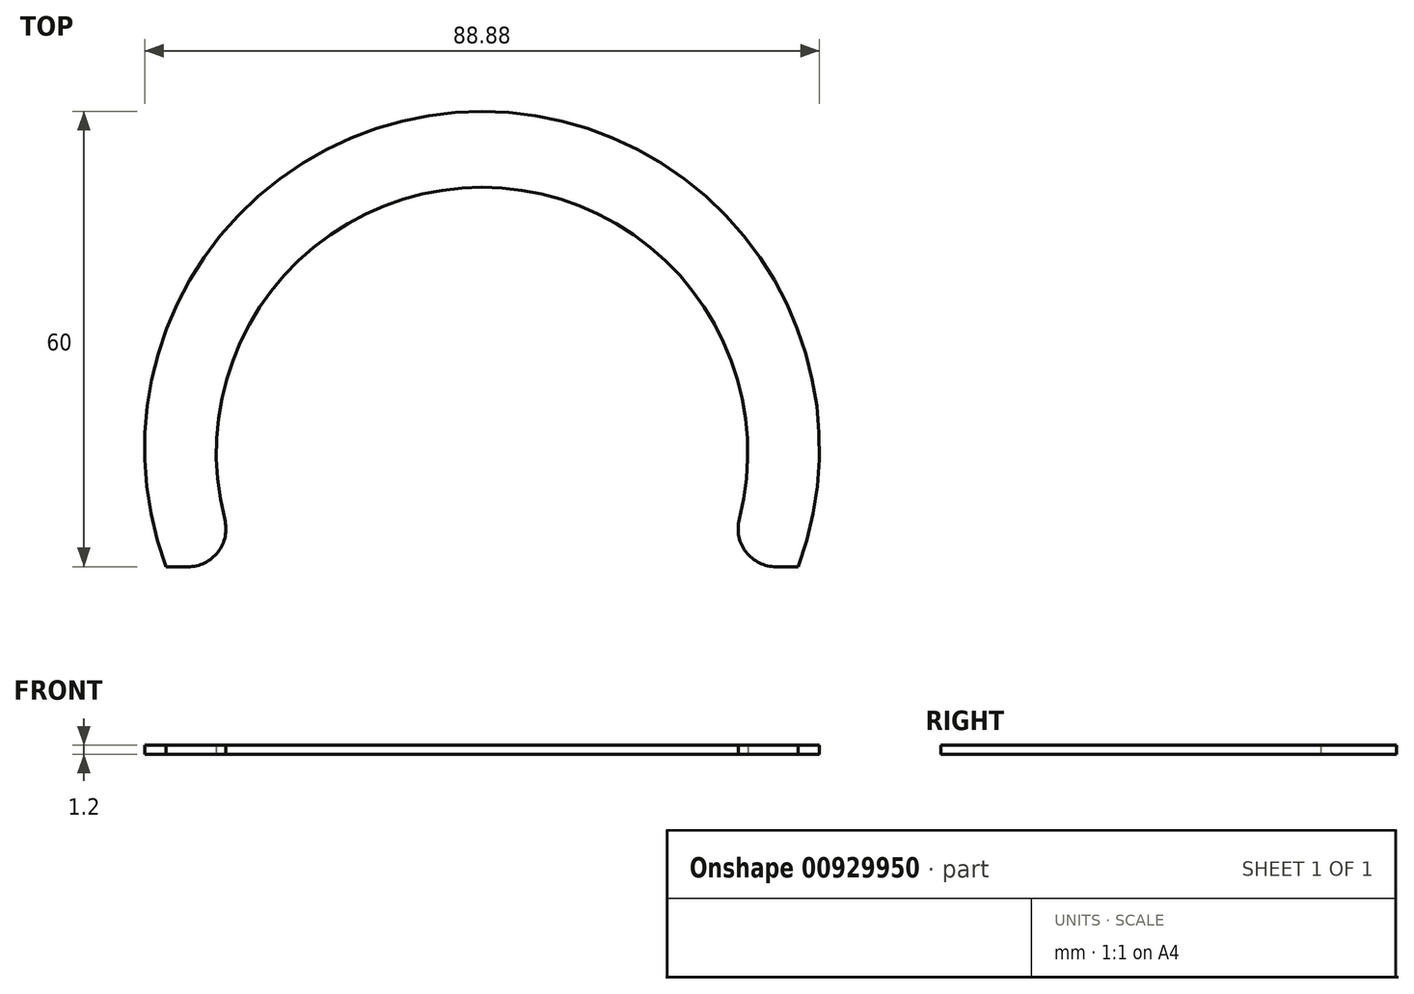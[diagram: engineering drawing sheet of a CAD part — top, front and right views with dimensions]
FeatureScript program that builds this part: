
annotation { "Feature Type Name" : "Feature", "Feature Type Description" : "" }
export const myFeature = defineFeature(function(context is Context, id is Id, definition is map)
    precondition{}
    {
        {
            var Q0;
            Q0=qCreatedBy(makeId("Top.planeOp"),FACE);
            var sketch = newSketch(context, id + "F0", { "sketchPlane" : qUnion([Q0])});
            skCircle(sketch, "E0", {"center": v(0, 0) * mm, "radius": 35 * mm, "construction": true});
            skPoint(sketch, "E1", {"position": v(-35, 0) * mm});
            skPoint(sketch, "E2", {"position": v(35, 0) * mm});
            skPoint(sketch, "E3", {"position": v(0, 35) * mm});
            skArc(sketch, "E4", {"start": v(31.62, -15) * mm, "mid": v(0, 35) * mm, "end": v(-31.62, -15) * mm});
            skLineSegment(sketch, "E5", {"start": v(-31.62, -15) * mm, "end": v(31.62, -15) * mm, "construction": true});
            skLineSegment(sketch, "E6", {"start": v(0, 0) * mm, "end": v(0, -15) * mm, "construction": true});
            skLineSegment(sketch, "E7", {"start": v(-31.62, -15) * mm, "end": v(-41.62, -15) * mm});
            skLineSegment(sketch, "E8", {"start": v(31.62, -15) * mm, "end": v(41.62, -15) * mm});
            skLineSegment(sketch, "E9", {"start": v(0, 45) * mm, "end": v(0, 35) * mm, "construction": true});
            skArc(sketch, "E10", {"start": v(41.62, -15) * mm, "mid": v(0, 45) * mm, "end": v(-41.62, -15) * mm});
            skSolve(sketch);
        }
        {
            var Q0;
            Q0 = qSketchRegion(id + "F0", true);
            extrude(context, id + "F1", {"entities" : qUnion([Q0]), "depth" : 1.2 * mm, "offsetDistance" : 25 * mm});
        }
        {
            var Q0;
            Q0=makeQuery(id+"F1.opExtrude","CAP_FACE",FACE,{"disambiguationData":[OSD([sQuery(id+"F0.wireOp",EDGE,"E4"),sQuery(id+"F0.wireOp",EDGE,"E7"),sQuery(id+"F0.wireOp",EDGE,"E8"),sQuery(id+"F0.wireOp",EDGE,"E10")])],"isStart":false});
            var sketch = newSketch(context, id + "F2", { "sketchPlane" : qUnion([Q0])});
            skArc(sketch, "E11.0", {"start": v(31.62, -15) * mm, "mid": v(0, 35) * mm, "end": v(-31.62, -15) * mm});
            skLineSegment(sketch, "E12", {"start": v(-31.62, -15) * mm, "end": v(-32.82, -15) * mm});
            skLineSegment(sketch, "E13", {"start": v(31.62, -15) * mm, "end": v(32.82, -15) * mm});
            skLineSegment(sketch, "E14", {"start": v(0, 35) * mm, "end": v(0, 36.2) * mm, "construction": true});
            skArc(sketch, "E15", {"start": v(32.82, -15) * mm, "mid": v(0, 36.2) * mm, "end": v(-32.82, -15) * mm});
            skSolve(sketch);
        }
        {
            var Q0;
            Q0 = qSketchRegion(id + "F2", true);
            extrude(context, id + "F3", {"entities" : qUnion([Q0]), "operationType" : NewBodyOperationType.ADD, "depth" : 10 * mm, "offsetDistance" : 25 * mm});
        }
        {
            var Q0;
            Q0=makeQuery(id+"F1.opExtrude","CAP_FACE",FACE,{"disambiguationData":[OSD([sQuery(id+"F0.wireOp",EDGE,"E4"),sQuery(id+"F0.wireOp",EDGE,"E7"),sQuery(id+"F0.wireOp",EDGE,"E8"),sQuery(id+"F0.wireOp",EDGE,"E10")])],"isStart":false});
            var sketch = newSketch(context, id + "F4", { "sketchPlane" : qUnion([Q0])});
            skArc(sketch, "E16.0", {"start": v(41.62, -15) * mm, "mid": v(0, 45) * mm, "end": v(-41.62, -15) * mm});
            skLineSegment(sketch, "E17", {"start": v(-41.62, -15) * mm, "end": v(-40.82, -15) * mm});
            skLineSegment(sketch, "E18", {"start": v(41.62, -15) * mm, "end": v(40.82, -15) * mm});
            skLineSegment(sketch, "E19", {"start": v(0, 45) * mm, "end": v(0, 44.2) * mm, "construction": true});
            skArc(sketch, "E20", {"start": v(40.82, -15) * mm, "mid": v(0, 44.2) * mm, "end": v(-40.82, -15) * mm});
            skSolve(sketch);
        }
        {
            var Q0;
            Q0 = qSketchRegion(id + "F4", true);
            extrude(context, id + "F5", {"entities" : qUnion([Q0]), "operationType" : NewBodyOperationType.ADD, "depth" : 135 * mm, "offsetDistance" : 25 * mm});
        }
        {
            var Q0;
            Q0=makeQuery(id+"F3.boolean.opBoolean","MERGE",EDGE,{"derivedFrom":[makeQuery(id+"F1.opExtrude","SWEPT_EDGE",EDGE,{"disambiguationData":[OSD([sQuery(id+"F0.wireOp",EDGE,"E4"),sQuery(id+"F0.wireOp",EDGE,"E7")])]}),makeQuery(id+"F3.opExtrude","SWEPT_EDGE",EDGE,{"disambiguationData":[OSD([sQuery(id+"F2.wireOp",EDGE,"E11.0"),sQuery(id+"F2.wireOp",EDGE,"E12")])]})]});
            var Q1;
            Q1=makeQuery(id+"F3.boolean.opBoolean","MERGE",EDGE,{"derivedFrom":[makeQuery(id+"F1.opExtrude","SWEPT_EDGE",EDGE,{"disambiguationData":[OSD([sQuery(id+"F0.wireOp",EDGE,"E4"),sQuery(id+"F0.wireOp",EDGE,"E8")])]}),makeQuery(id+"F3.opExtrude","SWEPT_EDGE",EDGE,{"disambiguationData":[OSD([sQuery(id+"F2.wireOp",EDGE,"E11.0"),sQuery(id+"F2.wireOp",EDGE,"E13")])]})]});
            fillet(context, id + "F6", {"entities" : qUnion([Q0, Q1]), "radius" : 5 * mm, "tangentPropagation" : true, "allowEdgeOverflow" : false});
        }
        {
            var Q0;
            Q0=qCreatedBy(makeId("Top.planeOp"),FACE);
            var sketch = newSketch(context, id + "F7", { "sketchPlane" : qUnion([Q0])});
            skCircle(sketch, "E21", {"center": v(0, 0) * mm, "radius": 63.74 * mm});
            skSolve(sketch);
        }
        {
            var Q0;
            Q0 = qSketchRegion(id + "F7", true);
            var Q1;
            Q1=makeQuery(id+"F1.opExtrude","CAP_FACE",FACE,{"disambiguationData":[OSD([sQuery(id+"F0.wireOp",EDGE,"E4"),sQuery(id+"F0.wireOp",EDGE,"E7"),sQuery(id+"F0.wireOp",EDGE,"E8"),sQuery(id+"F0.wireOp",EDGE,"E10")])],"isStart":false});
            extrude(context, id + "F8", {"entities" : qUnion([Q0]), "endBound" : BoundingType.UP_TO_SURFACE, "depth" : 25 * mm, "endBoundEntityFace" : qUnion([Q1]), "offsetDistance" : 25 * mm});
        }
        {
            var Q0;
            Q0=makeQuery(id+"F8.opExtrude","SWEPT_BODY",BODY,{"disambiguationData":[OSD([sQuery(id+"F7.wireOp",EDGE,"E21")])]});
            var Q1;
            Q1=makeQuery(id+"F1.opExtrude","SWEPT_BODY",BODY,{"disambiguationData":[OSD([sQuery(id+"F0.wireOp",EDGE,"E4"),sQuery(id+"F0.wireOp",EDGE,"E7"),sQuery(id+"F0.wireOp",EDGE,"E8"),sQuery(id+"F0.wireOp",EDGE,"E10")])]});
            booleanBodies(context, id + "F9", {"operationType" : BooleanOperationType.INTERSECTION, "tools" : qUnion([Q0, Q1])});
        }
    });
